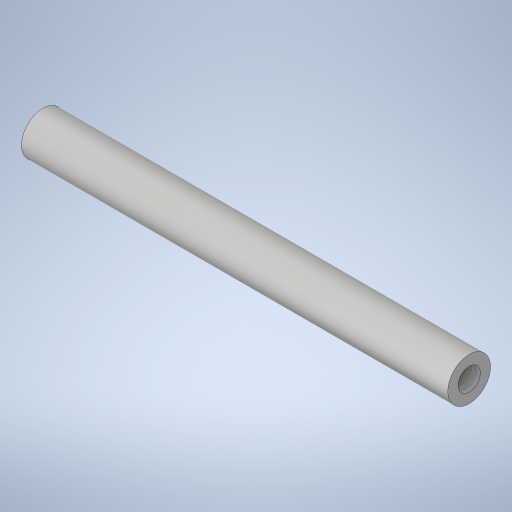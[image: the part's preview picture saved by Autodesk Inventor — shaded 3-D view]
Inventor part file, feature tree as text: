
AUTODESK INVENTOR PART (.ipt)
format: ipt  version: 2023.4 (Build 274418000, 418)  size: 256,512 bytes
history: native  units: in
note: dims shown in document units (in); Inventor stores cm internally (conversion verified against a paired STEP export)
features: sketch x2, extrude x1, hole x1
ambient origin geometry x8: Origin, YZ Plane, XZ Plane, XY Plane, X Axis, Y Axis, Z Axis, Center Point
bodies: Solid1 (feature_tree)
feature tree (4):
  extrude  "Extrusion1"  Depth=2.5in TaperAngle=0.0deg
  hole  "Hole1"  [1 undecoded]
  sketch  "Sketch1"  dims[d0=0.25in d1=2.5in d2=0.0in]
  sketch  "Sketch2"  dims[d3=0.13in d4=0.328in d5=0.385in d6=0.25in d7=0.5635in d8=1.0in d9=0.8108in]
note: 1 required parameter value undecoded (feature->parameter linkage not recoverable at this tier; creation-order binding heuristic only, values carry confidence <= 0.55)
